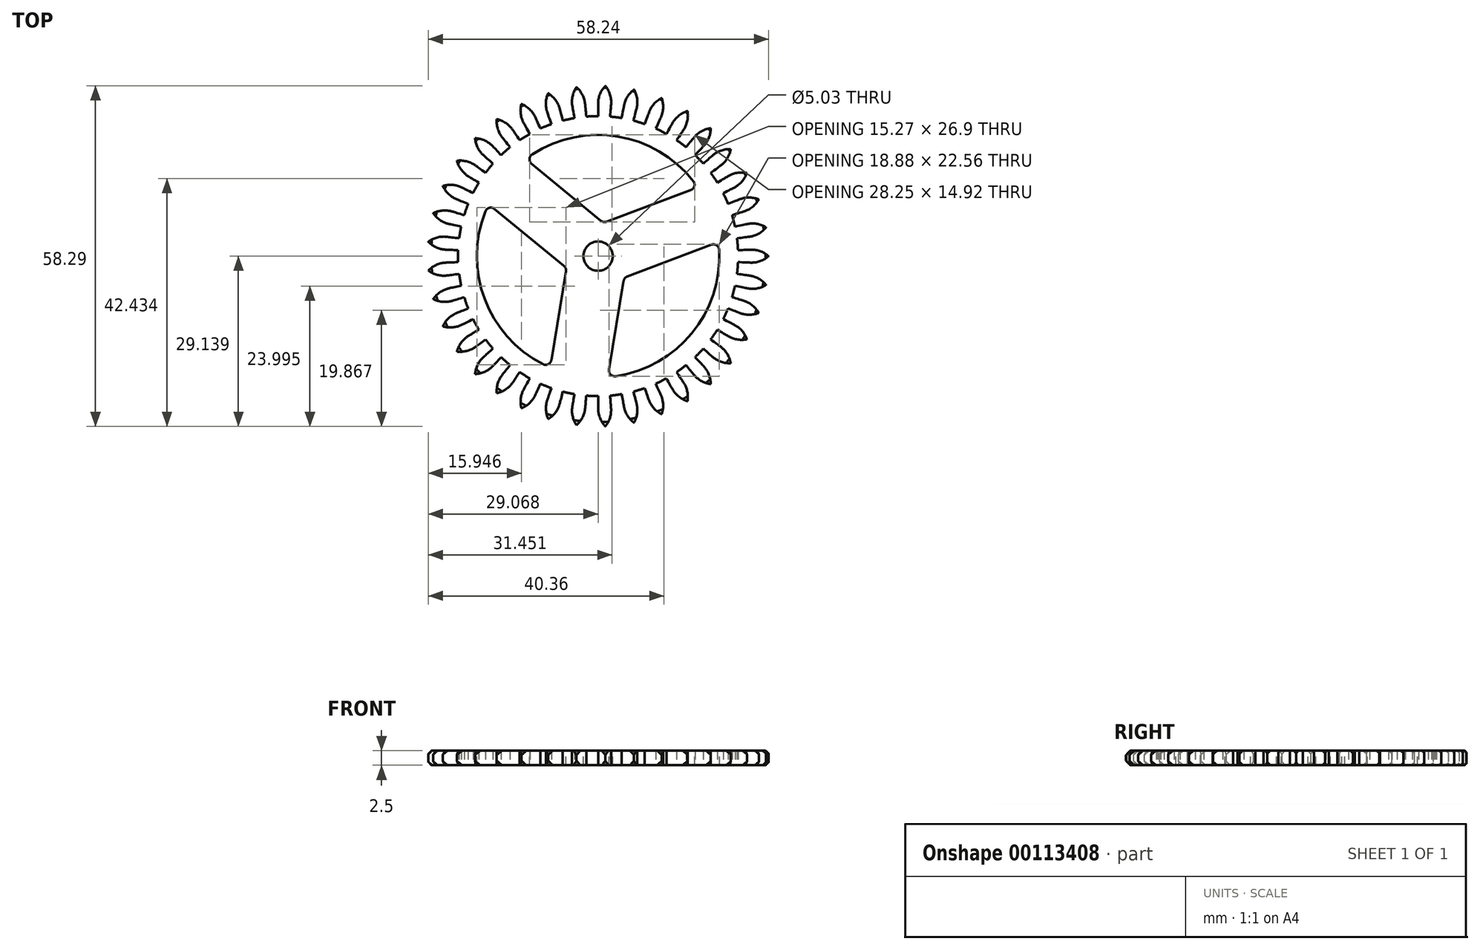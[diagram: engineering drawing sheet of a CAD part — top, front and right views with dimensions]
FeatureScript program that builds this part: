
annotation { "Feature Type Name" : "Feature", "Feature Type Description" : "" }
export const myFeature = defineFeature(function(context is Context, id is Id, definition is map)
    precondition{}
    {
        {
            var Q0;
            Q0=qCreatedBy(makeId("Top.planeOp"),FACE);
            var sketch = newSketch(context, id + "F0", { "sketchPlane" : qUnion([Q0])});
            skArc(sketch, "E0", {"start": v(18.04, 23.4) * mm, "mid": v(17.04, 23.55) * mm, "end": v(16.03, 23.66) * mm});
            skFitSpline(sketch, "E1", {"points": [v(14, 23.74) * mm, v(14, 25.61) * mm, v(14, 26.12) * mm, v(14.03, 26.38) * mm, v(14.12, 26.9) * mm, v(14.37, 27.63) * mm, v(14.75, 28.32) * mm, v(15.23, 28.93) * mm], "startDerivative": vector(0, 9.34) * mm, "endDerivative": vector(3.44, 4.02) * mm});
            skFitSpline(sketch, "E2", {"points": [v(16.03, 23.66) * mm, v(16.18, 25.42) * mm, v(16.22, 25.92) * mm, v(16.22, 26.18) * mm, v(16.18, 26.7) * mm, v(16.01, 27.46) * mm, v(15.72, 28.18) * mm, v(15.45, 28.63) * mm, v(15.23, 28.93) * mm], "startDerivative": vector(0.81, 9.65) * mm, "endDerivative": vector(-2.27, 3) * mm});
            skArc(sketch, "E3.trimOffspring", {"start": v(14, 23.75) * mm, "mid": v(14, 23.75) * mm, "end": v(13.99, 23.75) * mm});
            skLineSegment(sketch, "E4", {"start": v(13.99, 1.03) * mm, "end": v(14, 23.75) * mm});
            skLineSegment(sketch, "E5", {"start": v(18.04, 23.4) * mm, "end": v(14.2, 1.02) * mm});
            skLineSegment(sketch, "E6", {"start": v(13.99, 1.03) * mm, "end": v(13.99, -0.22) * mm});
            skLineSegment(sketch, "E7", {"start": v(14.2, 1.02) * mm, "end": v(13.99, -0.22) * mm});
            skSolve(sketch);
        }
        {
            var Q0;
            Q0 = qSketchRegion(id + "F0", true);
            extrude(context, id + "F1", {"entities" : qUnion([Q0]), "depth" : 2.5 * mm});
        }
        {
            var Q0;
            Q0=makeQuery(id+"F1.opExtrude","SWEPT_BODY",BODY,{"disambiguationData":[OSD([sQuery(id+"F0.wireOp",EDGE,"E0"),sQuery(id+"F0.wireOp",EDGE,"E1"),sQuery(id+"F0.wireOp",EDGE,"E2"),sQuery(id+"F0.wireOp",EDGE,"E4"),sQuery(id+"F0.wireOp",EDGE,"E5"),sQuery(id+"F0.wireOp",EDGE,"E6"),sQuery(id+"F0.wireOp",EDGE,"E7")])]});
            var Q1;
            Q1=makeQuery(id+"F1.opExtrude","SWEPT_EDGE",EDGE,{"disambiguationData":[OSD([sQuery(id+"F0.wireOp",EDGE,"E6"),sQuery(id+"F0.wireOp",EDGE,"E7")])]});
            circularPattern(context, id + "F2", {"operationType" : NewBodyOperationType.ADD, "entities" : qUnion([Q0]), "axis" : qUnion([Q1]), "angle" : 9.73 * degree, "instanceCount" : 38});
        }
        {
            var Q0;
            {var subQ0=makeQuery(id+"F1.opExtrude","CAP_FACE",FACE,{"disambiguationData":[OSD([sQuery(id+"F0.wireOp",EDGE,"E0"),sQuery(id+"F0.wireOp",EDGE,"E1"),sQuery(id+"F0.wireOp",EDGE,"E2"),sQuery(id+"F0.wireOp",EDGE,"E4"),sQuery(id+"F0.wireOp",EDGE,"E5"),sQuery(id+"F0.wireOp",EDGE,"E6"),sQuery(id+"F0.wireOp",EDGE,"E7")])],"isStart":false});Q0=makeQuery(id+"F2.boolean.opBoolean","MERGE",FACE,{"derivedFrom":[subQ0,makeQuery(id+"F2.opPattern","COPY",FACE,{"derivedFrom":subQ0,"instanceName":"1"}),makeQuery(id+"F2.opPattern","COPY",FACE,{"derivedFrom":subQ0,"instanceName":"2"}),makeQuery(id+"F2.opPattern","COPY",FACE,{"derivedFrom":subQ0,"instanceName":"3"}),makeQuery(id+"F2.opPattern","COPY",FACE,{"derivedFrom":subQ0,"instanceName":"4"}),makeQuery(id+"F2.opPattern","COPY",FACE,{"derivedFrom":subQ0,"instanceName":"5"}),makeQuery(id+"F2.opPattern","COPY",FACE,{"derivedFrom":subQ0,"instanceName":"6"}),makeQuery(id+"F2.opPattern","COPY",FACE,{"derivedFrom":subQ0,"instanceName":"7"}),makeQuery(id+"F2.opPattern","COPY",FACE,{"derivedFrom":subQ0,"instanceName":"8"}),makeQuery(id+"F2.opPattern","COPY",FACE,{"derivedFrom":subQ0,"instanceName":"9"}),makeQuery(id+"F2.opPattern","COPY",FACE,{"derivedFrom":subQ0,"instanceName":"10"}),makeQuery(id+"F2.opPattern","COPY",FACE,{"derivedFrom":subQ0,"instanceName":"11"}),makeQuery(id+"F2.opPattern","COPY",FACE,{"derivedFrom":subQ0,"instanceName":"12"}),makeQuery(id+"F2.opPattern","COPY",FACE,{"derivedFrom":subQ0,"instanceName":"13"}),makeQuery(id+"F2.opPattern","COPY",FACE,{"derivedFrom":subQ0,"instanceName":"14"}),makeQuery(id+"F2.opPattern","COPY",FACE,{"derivedFrom":subQ0,"instanceName":"15"}),makeQuery(id+"F2.opPattern","COPY",FACE,{"derivedFrom":subQ0,"instanceName":"16"}),makeQuery(id+"F2.opPattern","COPY",FACE,{"derivedFrom":subQ0,"instanceName":"17"}),makeQuery(id+"F2.opPattern","COPY",FACE,{"derivedFrom":subQ0,"instanceName":"18"}),makeQuery(id+"F2.opPattern","COPY",FACE,{"derivedFrom":subQ0,"instanceName":"19"}),makeQuery(id+"F2.opPattern","COPY",FACE,{"derivedFrom":subQ0,"instanceName":"20"}),makeQuery(id+"F2.opPattern","COPY",FACE,{"derivedFrom":subQ0,"instanceName":"21"}),makeQuery(id+"F2.opPattern","COPY",FACE,{"derivedFrom":subQ0,"instanceName":"22"}),makeQuery(id+"F2.opPattern","COPY",FACE,{"derivedFrom":subQ0,"instanceName":"23"}),makeQuery(id+"F2.opPattern","COPY",FACE,{"derivedFrom":subQ0,"instanceName":"24"}),makeQuery(id+"F2.opPattern","COPY",FACE,{"derivedFrom":subQ0,"instanceName":"25"}),makeQuery(id+"F2.opPattern","COPY",FACE,{"derivedFrom":subQ0,"instanceName":"26"}),makeQuery(id+"F2.opPattern","COPY",FACE,{"derivedFrom":subQ0,"instanceName":"27"}),makeQuery(id+"F2.opPattern","COPY",FACE,{"derivedFrom":subQ0,"instanceName":"28"}),makeQuery(id+"F2.opPattern","COPY",FACE,{"derivedFrom":subQ0,"instanceName":"29"}),makeQuery(id+"F2.opPattern","COPY",FACE,{"derivedFrom":subQ0,"instanceName":"30"}),makeQuery(id+"F2.opPattern","COPY",FACE,{"derivedFrom":subQ0,"instanceName":"31"}),makeQuery(id+"F2.opPattern","COPY",FACE,{"derivedFrom":subQ0,"instanceName":"32"}),makeQuery(id+"F2.opPattern","COPY",FACE,{"derivedFrom":subQ0,"instanceName":"33"}),makeQuery(id+"F2.opPattern","COPY",FACE,{"derivedFrom":subQ0,"instanceName":"34"}),makeQuery(id+"F2.opPattern","COPY",FACE,{"derivedFrom":subQ0,"instanceName":"35"}),makeQuery(id+"F2.opPattern","COPY",FACE,{"derivedFrom":subQ0,"instanceName":"36"}),makeQuery(id+"F2.opPattern","COPY",FACE,{"derivedFrom":subQ0,"instanceName":"37"})]});}
            var sketch = newSketch(context, id + "F3", { "sketchPlane" : qUnion([Q0])});
            skLineSegment(sketch, "E8", {"start": v(-9.96, -0.22) * mm, "end": v(-15.18, -0.22) * mm});
            skLineSegment(sketch, "E9", {"start": v(-15.18, -0.22) * mm, "end": v(43.16, -0.22) * mm, "construction": true});
            skCircle(sketch, "E10", {"center": v(13.99, -0.22) * mm, "radius": 2.52 * mm});
            skArc(sketch, "E11", {"start": v(-5.3, 7.46) * mm, "mid": v(-5.44, -7.53) * mm, "end": v(4.54, -18.7) * mm});
            skLineSegment(sketch, "E12", {"start": v(13.99, -0.22) * mm, "end": v(-2.06, 12.95) * mm, "construction": true});
            skLineSegment(sketch, "E13", {"start": v(13.99, -0.22) * mm, "end": v(10.6, -20.7) * mm, "construction": true});
            skLineSegment(sketch, "E14", {"start": v(13.99, -0.22) * mm, "end": v(33.42, 7.09) * mm, "construction": true});
            skLineSegment(sketch, "E15.0", {"start": v(8.14, -1.89) * mm, "end": v(-3.74, 7.86) * mm});
            skLineSegment(sketch, "E15.1", {"start": v(8.49, -2.82) * mm, "end": v(5.98, -17.98) * mm});
            skLineSegment(sketch, "E16.0", {"start": v(14.48, 5.84) * mm, "end": v(2.6, 15.59) * mm});
            skLineSegment(sketch, "E16.1", {"start": v(15.47, 5.68) * mm, "end": v(29.85, 11.09) * mm});
            skLineSegment(sketch, "E17.0", {"start": v(19, -3.68) * mm, "end": v(33.37, 1.73) * mm});
            skLineSegment(sketch, "E17.1", {"start": v(18.36, -4.45) * mm, "end": v(15.85, -19.61) * mm});
            skArc(sketch, "E18.trimOffspring", {"start": v(30.28, 12.64) * mm, "mid": v(17.37, 20.26) * mm, "end": v(2.7, 17.2) * mm});
            skArc(sketch, "E19.trimOffspring", {"start": v(16.98, -20.76) * mm, "mid": v(30.03, -13.4) * mm, "end": v(34.72, 0.84) * mm});
            skPoint(sketch, "E20.visualSharp", {"position": v(-4.76, 8.7) * mm});
            skArc(sketch, "E20.filletArc", {"start": v(-3.74, 7.86) * mm, "mid": v(-4.62, 8.06) * mm, "end": v(-5.3, 7.46) * mm});
            skPoint(sketch, "E21.visualSharp", {"position": v(5.77, -19.28) * mm});
            skArc(sketch, "E21.filletArc", {"start": v(4.54, -18.7) * mm, "mid": v(5.45, -18.71) * mm, "end": v(5.98, -17.98) * mm});
            skPoint(sketch, "E22.visualSharp", {"position": v(8.58, -2.25) * mm});
            skArc(sketch, "E22.filletArc", {"start": v(8.49, -2.82) * mm, "mid": v(8.44, -2.3) * mm, "end": v(8.14, -1.89) * mm});
            skPoint(sketch, "E23.visualSharp", {"position": v(14.93, 5.47) * mm});
            skArc(sketch, "E23.filletArc", {"start": v(14.48, 5.84) * mm, "mid": v(14.95, 5.63) * mm, "end": v(15.47, 5.68) * mm});
            skPoint(sketch, "E24.visualSharp", {"position": v(1.59, 16.43) * mm});
            skArc(sketch, "E24.filletArc", {"start": v(2.7, 17.2) * mm, "mid": v(2.25, 16.42) * mm, "end": v(2.6, 15.59) * mm});
            skPoint(sketch, "E25.visualSharp", {"position": v(31.09, 11.55) * mm});
            skArc(sketch, "E25.filletArc", {"start": v(29.85, 11.09) * mm, "mid": v(30.46, 11.75) * mm, "end": v(30.28, 12.64) * mm});
            skPoint(sketch, "E26.visualSharp", {"position": v(18.45, -3.88) * mm});
            skArc(sketch, "E26.filletArc", {"start": v(19, -3.68) * mm, "mid": v(18.57, -3.98) * mm, "end": v(18.36, -4.45) * mm});
            skPoint(sketch, "E27.visualSharp", {"position": v(34.6, 2.2) * mm});
            skArc(sketch, "E27.filletArc", {"start": v(34.72, 0.84) * mm, "mid": v(34.27, 1.63) * mm, "end": v(33.37, 1.73) * mm});
            skPoint(sketch, "E28.visualSharp", {"position": v(15.63, -20.92) * mm});
            skArc(sketch, "E28.filletArc", {"start": v(15.85, -19.61) * mm, "mid": v(16.12, -20.47) * mm, "end": v(16.98, -20.76) * mm});
            skSolve(sketch);
        }
        {
            var Q0;
            Q0 = qSketchRegion(id + "F3", true);
            extrude(context, id + "F4", {"entities" : qUnion([Q0]), "operationType" : NewBodyOperationType.REMOVE, "endBound" : BoundingType.THROUGH_ALL, "oppositeDirection" : true, "depth" : 25 * mm});
        }
        {
            var Q0;
            Q0=qCreatedBy(makeId("Front.planeOp"),FACE);
            var sketch = newSketch(context, id + "F5", { "sketchPlane" : qUnion([Q0])});
            skLineSegment(sketch, "E29", {"start": v(-15.08, 2) * mm, "end": v(-16.35, 2) * mm, "construction": true});
            skLineSegment(sketch, "E30", {"start": v(-15.08, 0.5) * mm, "end": v(-16.54, 0.5) * mm, "construction": true});
            skLineSegment(sketch, "E31", {"start": v(-15.83, 1.25) * mm, "end": v(-14.58, 0) * mm});
            skLineSegment(sketch, "E32", {"start": v(-14.58, 2.5) * mm, "end": v(-15.83, 1.25) * mm});
            skPoint(sketch, "E33.orphan", {"position": v(-9.78, 2.5) * mm});
            skPoint(sketch, "E34.orphan", {"position": v(-9.78, 0) * mm});
            skLineSegment(sketch, "E35.bottom", {"start": v(-14.58, 2.5) * mm, "end": v(-17.64, 2.5) * mm});
            skLineSegment(sketch, "E35.top", {"start": v(-14.58, 0) * mm, "end": v(-17.64, 0) * mm});
            skLineSegment(sketch, "E35.right", {"start": v(-17.64, 2.5) * mm, "end": v(-17.64, 0) * mm});
            skLineSegment(sketch, "E36", {"start": v(-15.08, 0.5) * mm, "end": v(-15.08, 2) * mm, "construction": true});
            skLineSegment(sketch, "E37", {"start": v(14.04, 0) * mm, "end": v(14.04, 6.58) * mm, "construction": true});
            skSolve(sketch);
        }
        {
            var Q0;
            Q0 = qSketchRegion(id + "F5", true);
            var Q1;
            Q1=sQuery(id+"F5.wireOp",EDGE,"E37");
            revolve(context, id + "F6", {"operationType" : NewBodyOperationType.REMOVE, "entities" : qUnion([Q0]), "axis" : qUnion([Q1]), "revolveType" : RevolveType.FULL, "oppositeDirection" : true});
        }
    });
